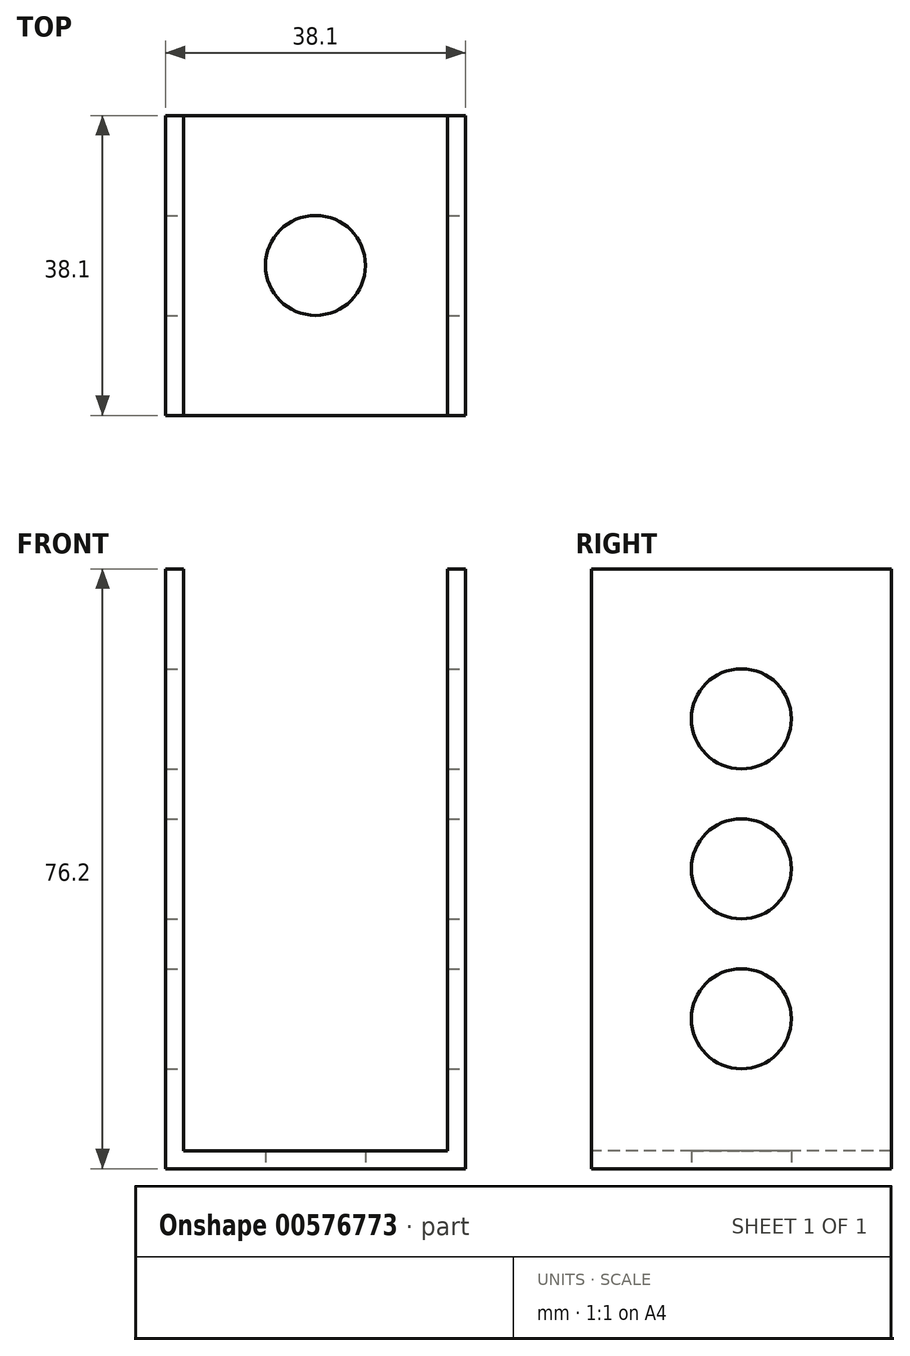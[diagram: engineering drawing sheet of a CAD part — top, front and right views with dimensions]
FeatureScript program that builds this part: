
annotation { "Feature Type Name" : "Feature", "Feature Type Description" : "" }
export const myFeature = defineFeature(function(context is Context, id is Id, definition is map)
    precondition{}
    {
        {
            var Q0;
            Q0=qCreatedBy(makeId("Top.planeOp"),FACE);
            var sketch = newSketch(context, id + "F0", { "sketchPlane" : qUnion([Q0])});
            skLineSegment(sketch, "E0.bottom", {"start": v(-15.9, 17.6) * mm, "end": v(22.2, 17.6) * mm});
            skLineSegment(sketch, "E0.top", {"start": v(-15.9, -20.5) * mm, "end": v(22.2, -20.5) * mm});
            skLineSegment(sketch, "E0.left", {"start": v(-15.9, 17.6) * mm, "end": v(-15.9, -20.5) * mm});
            skLineSegment(sketch, "E0.right", {"start": v(22.2, 17.6) * mm, "end": v(22.2, -20.5) * mm});
            skLineSegment(sketch, "E1.bottom", {"start": v(-15.9, 17.6) * mm, "end": v(-13.6, 17.6) * mm});
            skLineSegment(sketch, "E1.top", {"start": v(-15.9, -20.5) * mm, "end": v(-13.6, -20.5) * mm});
            skLineSegment(sketch, "E1.right", {"start": v(-13.6, 17.6) * mm, "end": v(-13.6, -20.5) * mm});
            skLineSegment(sketch, "E2.bottom", {"start": v(22.2, 17.6) * mm, "end": v(19.92, 17.6) * mm});
            skLineSegment(sketch, "E2.top", {"start": v(22.2, -20.5) * mm, "end": v(19.92, -20.5) * mm});
            skLineSegment(sketch, "E2.right", {"start": v(19.92, 17.6) * mm, "end": v(19.92, -20.5) * mm});
            skCircle(sketch, "E3", {"center": v(3.16, -1.45) * mm, "radius": 6.35 * mm});
            skSolve(sketch);
        }
        {
            var Q0;
            Q0 = qSketchRegion(id + "F0", true);
            extrude(context, id + "F1", {"entities" : qUnion([Q0]), "depth" : 2.3 * mm, "offsetDistance" : 25.4 * mm});
        }
        {
            var Q0;
            Q0=makeQuery(id+"F1.opExtrude","CAP_FACE",FACE,{"disambiguationData":[OSD([sQuery(id+"F0.wireOp",EDGE,"E0.bottom"),sQuery(id+"F0.wireOp",EDGE,"E0.top"),sQuery(id+"F0.wireOp",EDGE,"E1.bottom"),sQuery(id+"F0.wireOp",EDGE,"E1.top"),sQuery(id+"F0.wireOp",EDGE,"E0.left"),sQuery(id+"F0.wireOp",EDGE,"E2.bottom"),sQuery(id+"F0.wireOp",EDGE,"E2.top"),sQuery(id+"F0.wireOp",EDGE,"E0.right"),sQuery(id+"F0.wireOp",EDGE,"E3")])],"isStart":false});
            var sketch = newSketch(context, id + "F2", { "sketchPlane" : qUnion([Q0])});
            skLineSegment(sketch, "E4.bottom", {"start": v(-15.9, 17.6) * mm, "end": v(-13.6, 17.6) * mm});
            skLineSegment(sketch, "E4.top", {"start": v(-15.9, -20.5) * mm, "end": v(-13.6, -20.5) * mm});
            skLineSegment(sketch, "E4.left", {"start": v(-15.9, 17.6) * mm, "end": v(-15.9, -20.5) * mm});
            skLineSegment(sketch, "E4.right", {"start": v(-13.6, 17.6) * mm, "end": v(-13.6, -20.5) * mm});
            skLineSegment(sketch, "E5.bottom", {"start": v(22.2, 17.6) * mm, "end": v(19.92, 17.6) * mm});
            skLineSegment(sketch, "E5.top", {"start": v(22.2, -20.5) * mm, "end": v(19.92, -20.5) * mm});
            skLineSegment(sketch, "E5.left", {"start": v(22.2, 17.6) * mm, "end": v(22.2, -20.5) * mm});
            skLineSegment(sketch, "E5.right", {"start": v(19.92, 17.6) * mm, "end": v(19.92, -20.5) * mm});
            skSolve(sketch);
        }
        {
            var Q0;
            Q0 = qSketchRegion(id + "F2", true);
            extrude(context, id + "F3", {"entities" : qUnion([Q0]), "operationType" : NewBodyOperationType.ADD, "depth" : 73.9 * mm, "offsetDistance" : 25.4 * mm});
        }
        {
            var Q0;
            Q0=makeQuery(id+"F3.boolean.opBoolean","MERGE",FACE,{"derivedFrom":[makeQuery(id+"F1.opExtrude","SWEPT_FACE",FACE,{"disambiguationData":[OSD([sQuery(id+"F0.wireOp",EDGE,"E0.right")])]}),makeQuery(id+"F3.opExtrude","SWEPT_FACE",FACE,{"disambiguationData":[OSD([sQuery(id+"F2.wireOp",EDGE,"E5.left")])]})]});
            var sketch = newSketch(context, id + "F4", { "sketchPlane" : qUnion([Q0])});
            skCircle(sketch, "E6", {"center": v(-1.45, 57.15) * mm, "radius": 6.35 * mm});
            skCircle(sketch, "E7", {"center": v(-1.45, 38.1) * mm, "radius": 6.35 * mm});
            skCircle(sketch, "E8", {"center": v(-1.45, 19.05) * mm, "radius": 6.35 * mm});
            skSolve(sketch);
        }
        {
            var Q0;
            Q0 = qSketchRegion(id + "F4", true);
            extrude(context, id + "F5", {"entities" : qUnion([Q0]), "operationType" : NewBodyOperationType.REMOVE, "endBound" : BoundingType.THROUGH_ALL, "oppositeDirection" : true, "depth" : 25.4 * mm, "offsetDistance" : 25.4 * mm});
        }
    });
